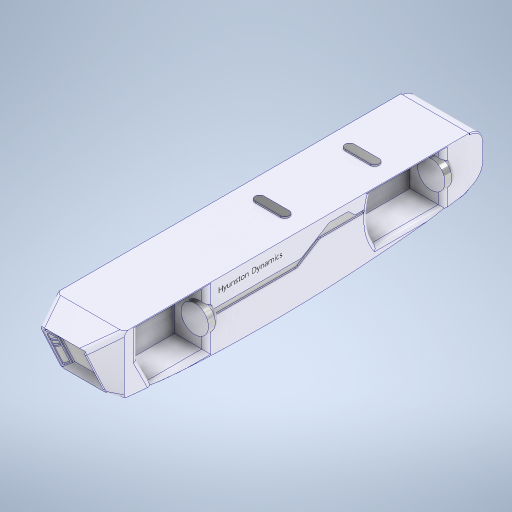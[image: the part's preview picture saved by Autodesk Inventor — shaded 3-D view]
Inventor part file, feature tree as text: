
AUTODESK INVENTOR PART (.ipt)
format: ipt  version: 2023 (Build 270158000, 158)  size: 1,555,968 bytes
history: native  units: mm
features: sketch x26, other x17, extrude x17, fillet x14, loft x4, projected_geometry x4
ambient origin geometry x8: Origin, YZ Plane, XZ Plane, XY Plane, X Axis, Y Axis, Z Axis, Center Point
bodies: Body1 (feature_tree)
feature tree (82):
  other  "솔리드1"
  sketch  "스케치1"
  other  "작업 평면2"
  loft  "로프트1"
  sketch  "스케치7"
  extrude  "돌출1"  Depth=125.0mm
  fillet  "모깎기1"  [1 undecoded]
  extrude  "돌출2"  Depth=150.0mm
  fillet  "모깎기2"  Radius=140.0mm
  extrude  "돌출3"  Depth=110.0mm
  extrude  "돌출4"  Depth=150.0mm
  fillet  "모깎기3"  [1 undecoded]
  extrude  "돌출5"  TaperAngle=0.0deg  [1 undecoded]
  fillet  "모깎기4"  [1 undecoded]
  extrude  "돌출6"  Depth=150.0mm
  extrude  "돌출7"  Depth=5.0mm
  fillet  "모깎기6"  Radius=120.0mm
  fillet  "모깎기7"  Radius=30.0mm
  sketch  "스케치16"
  extrude  "돌출8"  Depth=180.0mm
  other  "작업 평면4"
  loft  "로프트2"
  other  "면 모깎기1"
  other  "면 모깎기2"
  other  "면 모깎기3"
  fillet  "모깎기9"  Radius=30.0mm
  fillet  "모깎기10"  Radius=65.0mm
  extrude  "돌출10"  Depth=10.0mm
  fillet  "모깎기12"  Radius=60.0mm
  extrude  "돌출11"  Depth=50.0mm
  fillet  "모깎기14"  Radius=60.0mm
  sketch  "스케치19"
  other  "작업 평면7"
  sketch  "스케치22"
  loft  "로프트6"
  other  "작업 평면8"
  loft  "로프트7"
  sketch  "스케치24"
  extrude  "돌출12"  TaperAngle=0.0deg  [1 undecoded]
  extrude  "돌출13"  Depth=65.0mm TaperAngle=0.0deg
  extrude  "돌출14"  Depth=10.0mm
  extrude  "돌출16"  Depth=10.0mm TaperAngle=0.0deg
  fillet  "모깎기18"  Radius=10.0mm
  fillet  "모깎기19"  Radius=5.0mm
  fillet  "모깎기20"  Radius=5.0mm
  fillet  "모깎기21"  [1 undecoded]
  other  "전사1"
  extrude  "돌출17"  TaperAngle=0.0deg  [1 undecoded]
  other  "전사2"
  other  "작업 평면9"
  sketch  "스케치34"
  extrude  "돌출18"  Depth=10.0mm
  extrude  "돌출19"  Depth=1.0mm
  other  "작업 평면1"
  sketch  "스케치3"
  sketch  "스케치4"
  sketch  "스케치8"
  sketch  "스케치9"
  sketch  "스케치10"
  projected_geometry  "투영된 루프1"
  sketch  "스케치11"
  sketch  "스케치12"
  sketch  "스케치13"
  sketch  "스케치15"
  sketch  "스케치17"
  other  "모서리1"
  sketch  "스케치18"
  other  "작업 평면5"
  projected_geometry  "투영된 루프2"
  other  "모서리6"
  sketch  "스케치23"
  sketch  "스케치25"
  projected_geometry  "투영된 루프3"
  sketch  "스케치26"
  projected_geometry  "투영된 루프4"
  sketch  "스케치27"
  sketch  "스케치29"
  sketch  "스케치30"
  other  "이미지1"
  sketch  "스케치32"
  sketch  "스케치33"
  other  "이미지2"
note: 7 required parameter values undecoded (feature->parameter linkage not recoverable at this tier; creation-order binding heuristic only, values carry confidence <= 0.55)
